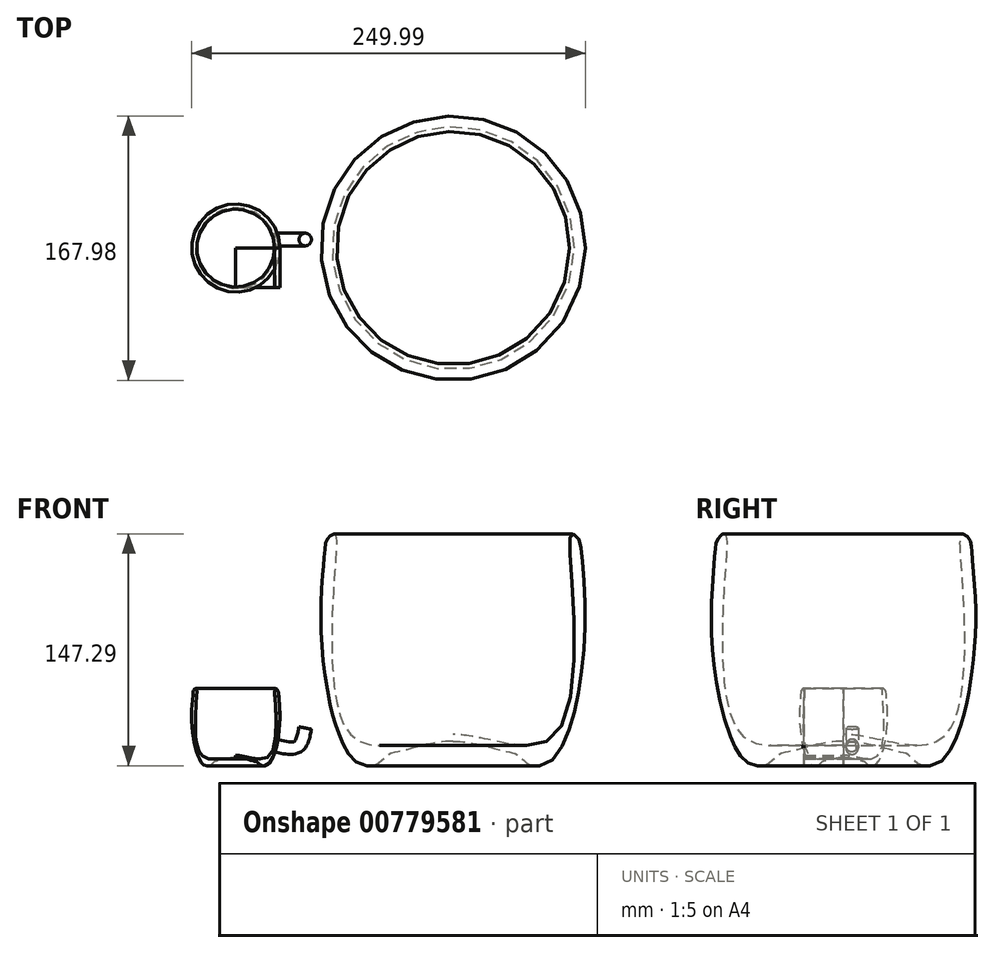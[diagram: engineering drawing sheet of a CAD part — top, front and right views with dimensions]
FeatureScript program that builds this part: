
annotation { "Feature Type Name" : "Feature", "Feature Type Description" : "" }
export const myFeature = defineFeature(function(context is Context, id is Id, definition is map)
    precondition{}
    {
        {
            var Q0;
            Q0=qCreatedBy(makeId("Front.planeOp"),FACE);
            var sketch = newSketch(context, id + "F0", { "sketchPlane" : qUnion([Q0])});
            skLineSegment(sketch, "E0", {"start": v(-16.4, 0) * mm, "end": v(16.4, 0) * mm, "construction": true});
            skLineSegment(sketch, "E1", {"start": v(0, -13.93) * mm, "end": v(0, 13.93) * mm, "construction": true});
            skLineSegment(sketch, "E2", {"start": v(0, 6.6) * mm, "end": v(0, 5.18) * mm});
            skLineSegment(sketch, "E3", {"start": v(17.23, 0) * mm, "end": v(18.25, 0) * mm});
            skLineSegment(sketch, "E4", {"start": v(0, 5.18) * mm, "end": v(6.14, 5.18) * mm, "construction": true});
            skFitSpline(sketch, "E5", {"points": [v(0, 5.18) * mm, v(2.77, 4.97) * mm, v(6.6, 4.26) * mm, v(11.46, 2.96) * mm, v(13.75, 2.25) * mm, v(17.23, 0) * mm], "startDerivative": vector(21.52, 0) * mm, "endDerivative": vector(22, 0) * mm});
            skFitSpline(sketch, "E6", {"points": [v(18.25, 0) * mm, v(23.56, 5.18) * mm, v(26.73, 16.65) * mm, v(27.99, 32.79) * mm, v(27.17, 45.5) * mm, v(26.63, 47.98) * mm, v(25.23, 49.1) * mm, v(24.83, 44.4) * mm, v(22.21, 7.2) * mm, v(9.75, 5.03) * mm, v(2.39, 6.45) * mm, v(0, 6.6) * mm], "startDerivative": vector(91.7, 0) * mm, "endDerivative": vector(-33.22, 1.72) * mm});
            skPoint(sketch, "E7", {"position": v(25.86, 12.25) * mm});
            skPoint(sketch, "E8", {"position": v(40.68, 12.76) * mm});
            skPoint(sketch, "E9", {"position": v(43.85, 20.28) * mm});
            skPoint(sketch, "E10", {"position": v(45.74, 28.84) * mm});
            skPoint(sketch, "E11", {"position": v(46.57, 38.17) * mm});
            skPoint(sketch, "E12", {"position": v(43.26, 44.78) * mm});
            skPoint(sketch, "E13", {"position": v(37, 44.83) * mm});
            skPoint(sketch, "E14", {"position": v(32.99, 41.35) * mm});
            skPoint(sketch, "E15", {"position": v(27.65, 39.78) * mm});
            skPoint(sketch, "E16", {"position": v(33.46, 10.77) * mm});
            skLineSegment(sketch, "E17", {"start": v(45.74, 28.84) * mm, "end": v(43.85, 20.28) * mm, "construction": true});
            skSolve(sketch);
        }
        {
            var Q0;
            Q0=makeQuery(id+"F0.imprint","IMPRINT",FACE,{"disambiguationData":[TD([[makeQuery(id+"F0.imprint","IMPRINT",EDGE,{"derivedFrom":sQuery(id+"F0.wireOp",EDGE,"E2")}),1.0]])]});
            var Q1;
            Q1=sQuery(id+"F0.wireOp",EDGE,"E1");
            revolve(context, id + "F1", {"surfaceOperationType" : NewSurfaceOperationType.NEW, "entities" : qUnion([Q0]), "axis" : qUnion([Q1]), "revolveType" : RevolveType.FULL});
        }
        {
            var Q0;
            Q0=makeQuery(id+"F1.opRevolve","SWEPT_BODY",BODY,{"disambiguationData":[OSD([sQuery(id+"F0.wireOp",EDGE,"E2"),sQuery(id+"F0.wireOp",EDGE,"E3"),sQuery(id+"F0.wireOp",EDGE,"E5"),sQuery(id+"F0.wireOp",EDGE,"E6")])]});
            var Q1;
            Q1=qCreatedBy(makeId("Origin.pointOp"),VERTEX);
            transform(context, id + "F2", {"entities" : qUnion([Q0]), "transformType" : TransformType.SCALE_UNIFORMLY, "scale" : 3, "scalePoint" : qUnion([Q1]), "makeCopy" : true});
        }
        {
            var Q0;
            Q0=makeQuery(id+"F2.opPattern","COPY",BODY,{"derivedFrom":makeQuery(id+"F1.opRevolve","SWEPT_BODY",BODY,{"disambiguationData":[OSD([sQuery(id+"F0.wireOp",EDGE,"E2"),sQuery(id+"F0.wireOp",EDGE,"E3"),sQuery(id+"F0.wireOp",EDGE,"E5"),sQuery(id+"F0.wireOp",EDGE,"E6")])]}),"instanceName":"1"});
            transform(context, id + "F3", {"entities" : qUnion([Q0]), "transformType" : TransformType.TRANSLATION_3D, "dx" : 138 * mm, "dy" : 0 * mm, "dz" : 0 * mm, "makeCopy" : false});
        }
        {
            var Q0;
            Q0=makeQuery(id+"F0.imprint","IMPRINT",FACE,{"disambiguationData":[TD([[makeQuery(id+"F0.imprint","IMPRINT",EDGE,{"derivedFrom":sQuery(id+"F0.wireOp",EDGE,"E2")}),1.0]])]});
            extrude(context, id + "F4", {"entities" : qUnion([Q0]), "depth" : 25 * mm, "offsetDistance" : 25 * mm});
        }
        {
            var Q0;
            Q0=makeQuery(id+"F4.opExtrude","CAP_FACE",FACE,{"disambiguationData":[OSD([sQuery(id+"F0.wireOp",EDGE,"E2"),sQuery(id+"F0.wireOp",EDGE,"E3"),sQuery(id+"F0.wireOp",EDGE,"E5"),sQuery(id+"F0.wireOp",EDGE,"E6")])],"isStart":false});
            var sketch = newSketch(context, id + "F5", { "sketchPlane" : qUnion([Q0])});
            skFitSpline(sketch, "E18.0", {"points": [v(18.25, 0) * mm, v(20.78, 0) * mm, v(24.34, 5.6) * mm, v(27.12, 16.84) * mm, v(28.53, 32.05) * mm, v(27.13, 45.2) * mm, v(27.04, 47.87) * mm, v(24.57, 50.03) * mm, v(24.73, 43.22) * mm, v(28.46, 1.51) * mm, v(9.7, 4.95) * mm, v(2.85, 6.56) * mm, v(0.52, 6.56) * mm, v(0, 6.6) * mm]});
            skPoint(sketch, "E19.0", {"position": v(26.73, 16.65) * mm});
            skPoint(sketch, "E20.0", {"position": v(23.56, 5.18) * mm});
            skLineSegment(sketch, "E21", {"start": v(26.73, 16.65) * mm, "end": v(59.82, 4.7) * mm, "construction": true});
            skSolve(sketch);
        }
        {
            var Q0;
            Q0=sQuery(id+"F5.wireOp",VERTEX,"E19.0");
            var Q1;
            Q1=sQuery(id+"F0.wireOp",VERTEX,"E6.2.internal");
            var Q2;
            Q2=sQuery(id+"F0.wireOp",VERTEX,"E6.1.internal");
            cPlane(context, id + "F6", {"entities" : qUnion([Q0, Q1, Q2]), "cplaneType" : CPlaneType.THREE_POINT, "offset" : 25 * mm, "width" : 150 * mm, "height" : 150 * mm});
        }
        {
            var Q0;
            Q0=qCreatedBy(id+"F6.planeOp",FACE);
            cPlane(context, id + "F7", {"entities" : qUnion([Q0]), "cplaneType" : CPlaneType.OFFSET, "offset" : 0.84 * mm, "oppositeDirection" : true, "width" : 150 * mm, "height" : 150 * mm});
        }
        {
            var Q0;
            Q0=qCreatedBy(id+"F7.planeOp",FACE);
            var sketch = newSketch(context, id + "F8", { "sketchPlane" : qUnion([Q0])});
            skLineSegment(sketch, "E22", {"start": v(-19.58, 24.2) * mm, "end": v(5.42, 24.2) * mm, "construction": true});
            skLineSegment(sketch, "E23", {"start": v(-45.25, 14.2) * mm, "end": v(-1.45, 14.2) * mm, "construction": true});
            skCircle(sketch, "E24", {"center": v(5.42, 19.2) * mm, "radius": 4 * mm});
            skSolve(sketch);
        }
        {
            var Q0;
            Q0=qCreatedBy(makeId("Top.planeOp"),FACE);
            cPlane(context, id + "F9", {"entities" : qUnion([Q0]), "cplaneType" : CPlaneType.OFFSET, "offset" : 25 * mm, "width" : 150 * mm, "height" : 150 * mm});
        }
        {
            var Q0;
            Q0=qCreatedBy(id+"F9.planeOp",FACE);
            var sketch = newSketch(context, id + "F10", { "sketchPlane" : qUnion([Q0])});
            skLineSegment(sketch, "E25.bottom", {"start": v(33.28, 21.02) * mm, "end": v(58.18, 21.02) * mm});
            skLineSegment(sketch, "E25.top", {"start": v(33.28, -26.46) * mm, "end": v(58.18, -26.46) * mm});
            skLineSegment(sketch, "E25.left", {"start": v(33.28, 21.02) * mm, "end": v(33.28, -26.46) * mm});
            skLineSegment(sketch, "E25.right", {"start": v(58.18, 21.02) * mm, "end": v(58.18, -26.46) * mm});
            skLineSegment(sketch, "E26.0", {"start": v(45.74, 0) * mm, "end": v(43.85, 0) * mm, "construction": true});
            skCircle(sketch, "E27", {"center": v(45.74, 0) * mm, "radius": 4.52 * mm});
            skSolve(sketch);
        }
        {
            var Q0;
            Q0=qCreatedBy(makeId("Front.planeOp"),FACE);
            var sketch = newSketch(context, id + "F11", { "sketchPlane" : qUnion([Q0])});
            skPoint(sketch, "E28.0", {"position": v(25.86, 12.25) * mm});
            skPoint(sketch, "E29.0", {"position": v(33.46, 10.77) * mm});
            skPoint(sketch, "E30.0", {"position": v(40.68, 12.76) * mm});
            skPoint(sketch, "E31.0", {"position": v(43.85, 20.28) * mm});
            skPoint(sketch, "E32.0", {"position": v(44.8, 25) * mm});
            skFitSpline(sketch, "E33", {"points": [v(25.86, 12.25) * mm, v(33.46, 10.77) * mm, v(40.68, 12.76) * mm, v(43.85, 20.28) * mm, v(44.8, 25) * mm], "startDerivative": vector(28.12, -7.72) * mm, "endDerivative": vector(3.88, 20.48) * mm});
            skSolve(sketch);
        }
        {
            var Q0;
            Q0=makeQuery(id+"F8.imprint","IMPRINT",FACE,{"disambiguationData":[TD([[makeQuery(id+"F8.imprint","IMPRINT",EDGE,{"derivedFrom":sQuery(id+"F8.wireOp",EDGE,"E24")}),1.0]])]});
            var Q1;
            Q1=sQuery(id+"F11.wireOp",EDGE,"E33");
            sweep(context, id + "F12", {"operationType" : NewBodyOperationType.ADD, "profiles" : qUnion([Q0]), "path" : qUnion([Q1])});
        }
    });
